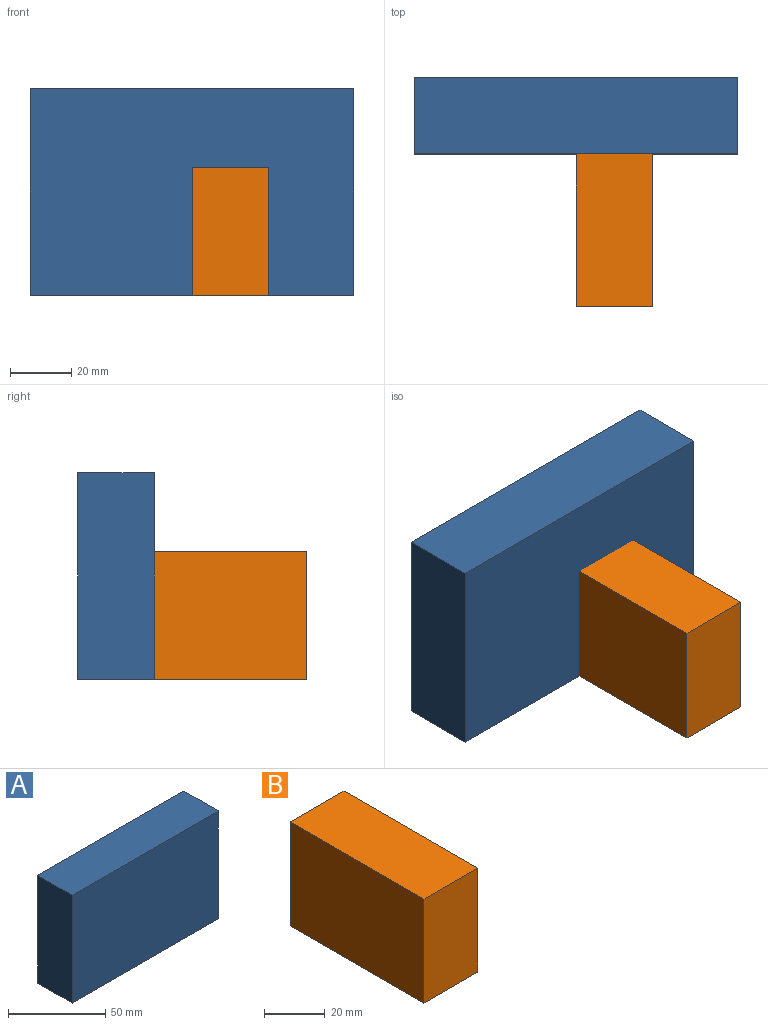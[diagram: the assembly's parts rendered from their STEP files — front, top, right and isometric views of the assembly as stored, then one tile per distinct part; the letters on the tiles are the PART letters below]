
ASSEMBLY  parts=2 mates=1
PART A: 6 faces, bbox 106.1x25x67.7 mm
  f0: plane 106.11x25mm, normal (0,0,1), area 2652.7mm2, adj f1,f3,f4,f5
  f1: plane 67.72x25mm, normal (-1,0,0), area 1693mm2, adj f0,f2,f4,f5
  f2: plane 106.11x25mm, normal (0,0,-1), area 2652.7mm2, adj f1,f3,f4,f5
  f3: plane 67.72x25mm, normal (1,0,0), area 1693mm2, adj f0,f2,f4,f5
  f4: plane 106.11x67.72mm, normal (0,-1,0), area 7185.9mm2, adj f0,f1,f2,f3
  f5: plane 106.11x67.72mm, normal (0,1,0), area 7185.9mm2, adj f0,f1,f2,f3
PART B: 6 faces, bbox 25x62.3x42 mm
  f0: plane 62.34x25mm, normal (0,0,1), area 1558.4mm2, adj f1,f3,f4,f5
  f1: plane 42.03x25mm, normal (0,-1,0), area 1050.7mm2, adj f0,f2,f4,f5
  f2: plane 62.34x25mm, normal (0,0,-1), area 1558.4mm2, adj f1,f3,f4,f5
  f3: plane 42.03x25mm, normal (0,1,0), area 1050.7mm2, adj f0,f2,f4,f5
  f4: plane 62.34x42.03mm, normal (1,0,0), area 2619.9mm2, adj f0,f1,f2,f3
  f5: plane 62.34x42.03mm, normal (-1,0,0), area 2619.9mm2, adj f0,f1,f2,f3
PLACE A t=(-12.4,9.04,-13.1)mm
PLACE B t=(-21.24,48.93,-12.26)mm
MATE planar B.f2 <-> A.f2  axis (0,0,-1) through (-21.24,-3.46,-20.66)mm
